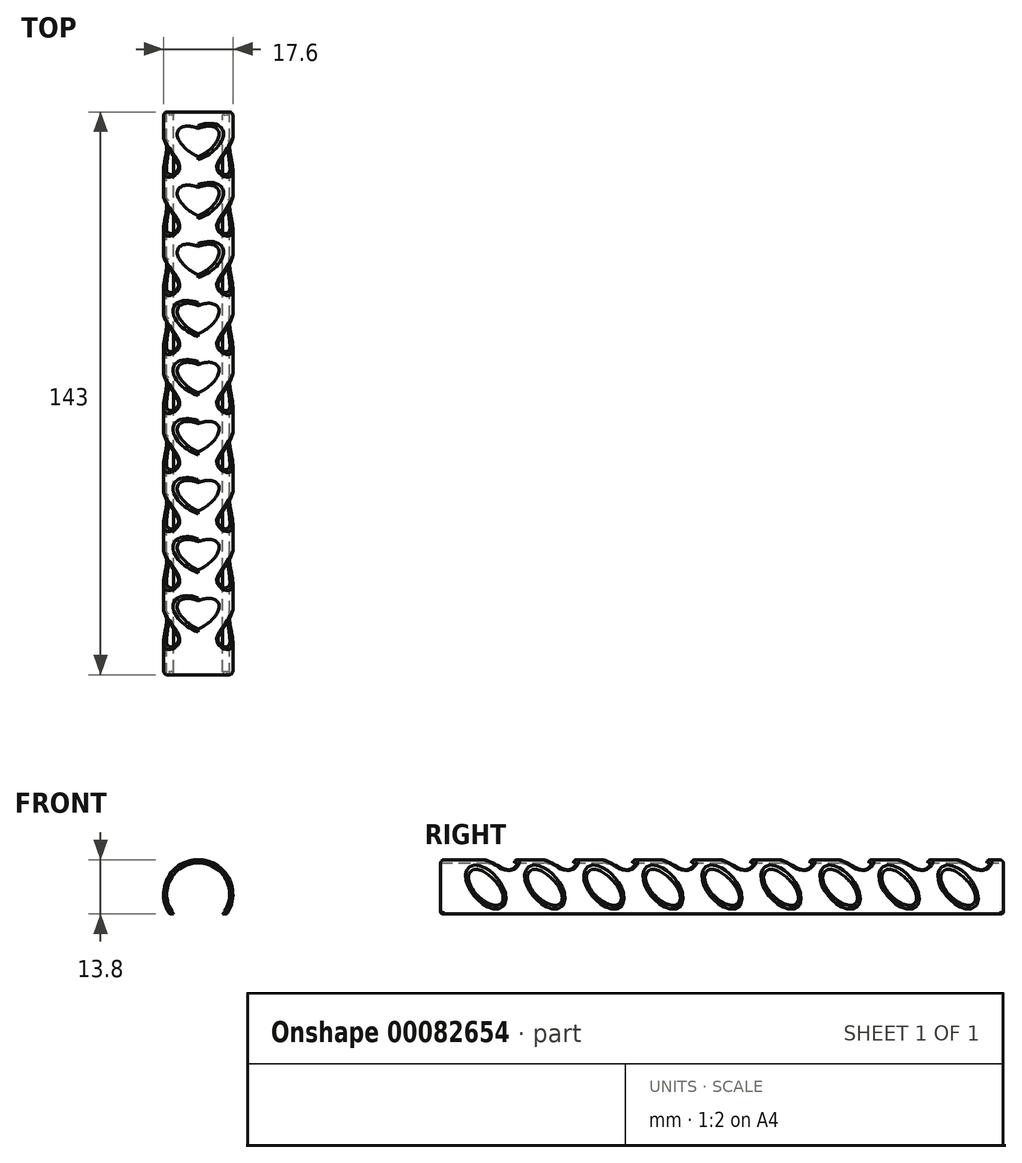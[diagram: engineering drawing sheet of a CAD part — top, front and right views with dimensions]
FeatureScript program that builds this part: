
annotation { "Feature Type Name" : "Feature", "Feature Type Description" : "" }
export const myFeature = defineFeature(function(context is Context, id is Id, definition is map)
    precondition{}
    {
        {
            var Q0;
            Q0=qCreatedBy(makeId("Front.planeOp"),FACE);
            var sketch = newSketch(context, id + "F0", { "sketchPlane" : qUnion([Q0])});
            skArc(sketch, "E0", {"start": v(6.24, -5) * mm, "mid": v(0, 8) * mm, "end": v(-6.24, -5) * mm});
            skArc(sketch, "E1", {"start": v(7.24, -5) * mm, "mid": v(0, 8.8) * mm, "end": v(-7.24, -5) * mm});
            skLineSegment(sketch, "E2", {"start": v(-7.24, -5) * mm, "end": v(-6.24, -5) * mm});
            skLineSegment(sketch, "E3.trimOffspring", {"start": v(6.24, -5) * mm, "end": v(7.24, -5) * mm});
            skSolve(sketch);
        }
        {
            var Q0;
            Q0 = qSketchRegion(id + "F0", true);
            extrude(context, id + "F1", {"entities" : qUnion([Q0]), "depth" : (143 / 2) * mm, "hasSecondDirection" : true, "secondDirectionOppositeDirection" : true, "secondDirectionDepth" : (143 / 2) * mm});
        }
        {
            var Q0;
            Q0=qCreatedBy(makeId("Right.planeOp"),FACE);
            var sketch = newSketch(context, id + "F2", { "sketchPlane" : qUnion([Q0])});
            skEllipse(sketch, "E4", {"center": v(0, 1.68) * mm, "majorRadius": 5.6 * mm, "minorRadius": 2.87 * mm, "majorAxis": v(0.7, -0.71)});
            skEllipse(sketch, "E5.1.0.0", {"center": v(15, 1.68) * mm, "majorRadius": 5.6 * mm, "minorRadius": 2.87 * mm, "majorAxis": v(0.7, -0.71)});
            skEllipse(sketch, "E5.2.0.0", {"center": v(30, 1.68) * mm, "majorRadius": 5.6 * mm, "minorRadius": 2.87 * mm, "majorAxis": v(0.7, -0.71)});
            skEllipse(sketch, "E5.3.0.0", {"center": v(45, 1.68) * mm, "majorRadius": 5.6 * mm, "minorRadius": 2.87 * mm, "majorAxis": v(0.7, -0.71)});
            skEllipse(sketch, "E5.4.0.0", {"center": v(60, 1.68) * mm, "majorRadius": 5.6 * mm, "minorRadius": 2.87 * mm, "majorAxis": v(0.7, -0.71)});
            skLineSegment(sketch, "E5.direction1", {"start": v(0, 1.68) * mm, "end": v(15, 1.68) * mm, "construction": true});
            skEllipse(sketch, "E6.1.0.0", {"center": v(-15, 1.68) * mm, "majorRadius": 5.6 * mm, "minorRadius": 2.87 * mm, "majorAxis": v(0.7, -0.71)});
            skEllipse(sketch, "E6.2.0.0", {"center": v(-30, 1.68) * mm, "majorRadius": 5.6 * mm, "minorRadius": 2.87 * mm, "majorAxis": v(0.7, -0.71)});
            skEllipse(sketch, "E6.3.0.0", {"center": v(-45, 1.68) * mm, "majorRadius": 5.6 * mm, "minorRadius": 2.87 * mm, "majorAxis": v(0.7, -0.71)});
            skEllipse(sketch, "E6.4.0.0", {"center": v(-60, 1.68) * mm, "majorRadius": 5.6 * mm, "minorRadius": 2.87 * mm, "majorAxis": v(0.7, -0.71)});
            skLineSegment(sketch, "E6.direction1", {"start": v(0, 1.68) * mm, "end": v(-15, 1.68) * mm, "construction": true});
            skSolve(sketch);
        }
        {
            var Q0;
            Q0 = qSketchRegion(id + "F2", true);
            extrude(context, id + "F3", {"entities" : qUnion([Q0]), "operationType" : NewBodyOperationType.REMOVE, "oppositeDirection" : true, "depth" : 25 * mm, "hasSecondDirection" : true, "secondDirectionOppositeDirection" : false, "secondDirectionDepth" : 25 * mm});
        }
        {
            var Q0;
            Q0=qCreatedBy(makeId("Top.planeOp"),FACE);
            var sketch = newSketch(context, id + "F4", { "sketchPlane" : qUnion([Q0])});
            skEllipticalArc(sketch, "E7", {});
            skLineSegment(sketch, "E8", {"start": v(0, 58.68) * mm, "end": v(0, 42.52) * mm, "construction": true});
            skEllipticalArc(sketch, "E9.MirrorCS", {});
            skEllipticalArc(sketch, "E10.0.1.0", {});
            skEllipticalArc(sketch, "E10.0.1.1", {});
            skEllipticalArc(sketch, "E10.0.2.0", {});
            skEllipticalArc(sketch, "E10.0.2.1", {});
            skEllipticalArc(sketch, "E10.0.3.0", {});
            skEllipticalArc(sketch, "E10.0.3.1", {});
            skEllipticalArc(sketch, "E10.0.4.0", {});
            skEllipticalArc(sketch, "E10.0.4.1", {});
            skEllipticalArc(sketch, "E10.0.5.0", {});
            skEllipticalArc(sketch, "E10.0.5.1", {});
            skEllipticalArc(sketch, "E10.0.6.0", {});
            skEllipticalArc(sketch, "E10.0.6.1", {});
            skEllipticalArc(sketch, "E10.0.7.0", {});
            skEllipticalArc(sketch, "E10.0.7.1", {});
            skLineSegment(sketch, "E10.direction1", {"start": v(0, 45.14) * mm, "end": v(25, 45.14) * mm, "construction": true});
            skLineSegment(sketch, "E10.direction2", {"start": v(0, 45.14) * mm, "end": v(0, 30.14) * mm, "construction": true});
            skEllipticalArc(sketch, "E11.0.1.0", {});
            skEllipticalArc(sketch, "E11.0.1.1", {});
            skLineSegment(sketch, "E11.direction2", {"start": v(0, 45.14) * mm, "end": v(0, 60.14) * mm, "construction": true});
            const initialGuessF4  = {"E7": [0, 0.04871673882007599, 0.8358285471048497, 0.5489905644404065, 0.005878045911660916, 0.003174595466172433, 4.371502825433306, 1.2299101718435133], "E9.MirrorCS": [0, 0.04871673882007599, -0.8358285471048497, 0.5489905644404065, 0.005878045911660916, 0.003174595466172433, 5.053275135336073, 1.91168248174628], "E10.0.1.0": [0, 0.03371673882007599, 0.8358285471048497, 0.5489905644404065, 0.005878045911660916, 0.003174595466172433, 4.371502825433306, 1.229910171843513], "E10.0.1.1": [0, 0.03371673882007599, -0.8358285471048497, 0.5489905644404065, 0.005878045911660916, 0.003174595466172433, 5.053275135336073, 1.91168248174628], "E10.0.2.0": [0, 0.01871673882007599, 0.8358285471048497, 0.5489905644404065, 0.005878045911660916, 0.003174595466172433, 4.371502825433306, 1.229910171843513], "E10.0.2.1": [0, 0.01871673882007599, -0.8358285471048497, 0.5489905644404065, 0.005878045911660916, 0.003174595466172433, 5.053275135336073, 1.91168248174628], "E10.0.3.0": [0, 0.0037167388200759904, 0.8358285471048497, 0.5489905644404065, 0.005878045911660916, 0.003174595466172433, 4.371502825433306, 1.229910171843513], "E10.0.3.1": [0, 0.0037167388200759904, -0.8358285471048497, 0.5489905644404065, 0.005878045911660916, 0.003174595466172433, 5.053275135336073, 1.91168248174628], "E10.0.4.0": [0, -0.011283261179924009, 0.8358285471048497, 0.5489905644404065, 0.005878045911660916, 0.003174595466172433, 4.371502825433306, 1.229910171843513], "E10.0.4.1": [0, -0.011283261179924009, -0.8358285471048497, 0.5489905644404065, 0.005878045911660916, 0.003174595466172433, 5.053275135336073, 1.91168248174628], "E10.0.5.0": [0, -0.02628326117992401, 0.8358285471048497, 0.5489905644404065, 0.005878045911660916, 0.003174595466172433, 4.371502825433306, 1.229910171843513], "E10.0.5.1": [0, -0.02628326117992401, -0.8358285471048497, 0.5489905644404065, 0.005878045911660916, 0.003174595466172433, 5.053275135336073, 1.91168248174628], "E10.0.6.0": [0, -0.04128326117992401, 0.8358285471048497, 0.5489905644404065, 0.005878045911660916, 0.003174595466172433, 4.371502825433306, 1.229910171843513], "E10.0.6.1": [0, -0.04128326117992401, -0.8358285471048497, 0.5489905644404065, 0.005878045911660916, 0.003174595466172433, 5.053275135336073, 1.91168248174628], "E10.0.7.0": [0, -0.05628326117992401, 0.8358285471048497, 0.5489905644404065, 0.005878045911660916, 0.003174595466172433, 4.371502825433306, 1.229910171843513], "E10.0.7.1": [0, -0.05628326117992401, -0.8358285471048497, 0.5489905644404065, 0.005878045911660916, 0.003174595466172433, 5.053275135336073, 1.91168248174628], "E11.0.1.0": [0, 0.06371673882007599, 0.8358285471048497, 0.5489905644404065, 0.005878045911660916, 0.003174595466172433, 4.371502825433306, 1.229910171843513], "E11.0.1.1": [0, 0.06371673882007599, -0.8358285471048497, 0.5489905644404065, 0.005878045911660916, 0.003174595466172433, 5.053275135336073, 1.91168248174628]};
            skSetInitialGuess(sketch, initialGuessF4);
            skSolve(sketch);
        }
        {
            var Q0;
            Q0 = qSketchRegion(id + "F4", true);
            extrude(context, id + "F5", {"entities" : qUnion([Q0]), "operationType" : NewBodyOperationType.REMOVE, "depth" : 25 * mm});
        }
        {
            var Q0;
            Q0=makeQuery(id+"F1.opExtrude","CAP_EDGE",EDGE,{"disambiguationData":[OSD([sQuery(id+"F0.wireOp",EDGE,"E1")])],"isStart":true});
            var Q1;
            Q1=makeQuery(id+"F1.opExtrude","CAP_EDGE",EDGE,{"disambiguationData":[OSD([sQuery(id+"F0.wireOp",EDGE,"E1")])],"isStart":false});
            fillet(context, id + "F6", {"entities" : qUnion([Q0, Q1]), "radius" : 1 * mm, "tangentPropagation" : true, "allowEdgeOverflow" : false});
        }
        {
            var Q0;
            Q0=makeQuery(id+"F3.boolean.opBoolean","INTERSECT",EDGE,{"disambiguationData":[OD(0.0)],"derivedFrom":[makeQuery(id+"F1.opExtrude","SWEPT_FACE",FACE,{"disambiguationData":[OSD([sQuery(id+"F0.wireOp",EDGE,"E1")])]}),makeQuery(id+"F3.opExtrude","SWEPT_FACE",FACE,{"disambiguationData":[OSD([sQuery(id+"F2.wireOp",EDGE,"E5.4.0.0")])]})]});
            var Q1;
            Q1=makeQuery(id+"F3.boolean.opBoolean","INTERSECT",EDGE,{"disambiguationData":[OD(0.0)],"derivedFrom":[makeQuery(id+"F1.opExtrude","SWEPT_FACE",FACE,{"disambiguationData":[OSD([sQuery(id+"F0.wireOp",EDGE,"E1")])]}),makeQuery(id+"F3.opExtrude","SWEPT_FACE",FACE,{"disambiguationData":[OSD([sQuery(id+"F2.wireOp",EDGE,"E5.3.0.0")])]})]});
            var Q2;
            Q2=makeQuery(id+"F3.boolean.opBoolean","INTERSECT",EDGE,{"disambiguationData":[OD(0.0)],"derivedFrom":[makeQuery(id+"F1.opExtrude","SWEPT_FACE",FACE,{"disambiguationData":[OSD([sQuery(id+"F0.wireOp",EDGE,"E1")])]}),makeQuery(id+"F3.opExtrude","SWEPT_FACE",FACE,{"disambiguationData":[OSD([sQuery(id+"F2.wireOp",EDGE,"E5.2.0.0")])]})]});
            var Q3;
            Q3=makeQuery(id+"F3.boolean.opBoolean","INTERSECT",EDGE,{"disambiguationData":[OD(0.0)],"derivedFrom":[makeQuery(id+"F1.opExtrude","SWEPT_FACE",FACE,{"disambiguationData":[OSD([sQuery(id+"F0.wireOp",EDGE,"E1")])]}),makeQuery(id+"F3.opExtrude","SWEPT_FACE",FACE,{"disambiguationData":[OSD([sQuery(id+"F2.wireOp",EDGE,"E5.1.0.0")])]})]});
            var Q4;
            Q4=makeQuery(id+"F3.boolean.opBoolean","INTERSECT",EDGE,{"disambiguationData":[OD(0.0)],"derivedFrom":[makeQuery(id+"F1.opExtrude","SWEPT_FACE",FACE,{"disambiguationData":[OSD([sQuery(id+"F0.wireOp",EDGE,"E1")])]}),makeQuery(id+"F3.opExtrude","SWEPT_FACE",FACE,{"disambiguationData":[OSD([sQuery(id+"F2.wireOp",EDGE,"E4")])]})]});
            var Q5;
            Q5=makeQuery(id+"F3.boolean.opBoolean","INTERSECT",EDGE,{"disambiguationData":[OD(0.0)],"derivedFrom":[makeQuery(id+"F1.opExtrude","SWEPT_FACE",FACE,{"disambiguationData":[OSD([sQuery(id+"F0.wireOp",EDGE,"E1")])]}),makeQuery(id+"F3.opExtrude","SWEPT_FACE",FACE,{"disambiguationData":[OSD([sQuery(id+"F2.wireOp",EDGE,"E6.1.0.0")])]})]});
            var Q6;
            Q6=makeQuery(id+"F3.boolean.opBoolean","INTERSECT",EDGE,{"disambiguationData":[OD(0.0)],"derivedFrom":[makeQuery(id+"F1.opExtrude","SWEPT_FACE",FACE,{"disambiguationData":[OSD([sQuery(id+"F0.wireOp",EDGE,"E1")])]}),makeQuery(id+"F3.opExtrude","SWEPT_FACE",FACE,{"disambiguationData":[OSD([sQuery(id+"F2.wireOp",EDGE,"E6.2.0.0")])]})]});
            var Q7;
            Q7=makeQuery(id+"F3.boolean.opBoolean","INTERSECT",EDGE,{"disambiguationData":[OD(0.0)],"derivedFrom":[makeQuery(id+"F1.opExtrude","SWEPT_FACE",FACE,{"disambiguationData":[OSD([sQuery(id+"F0.wireOp",EDGE,"E1")])]}),makeQuery(id+"F3.opExtrude","SWEPT_FACE",FACE,{"disambiguationData":[OSD([sQuery(id+"F2.wireOp",EDGE,"E6.3.0.0")])]})]});
            var Q8;
            Q8=makeQuery(id+"F3.boolean.opBoolean","INTERSECT",EDGE,{"disambiguationData":[OD(0.0)],"derivedFrom":[makeQuery(id+"F1.opExtrude","SWEPT_FACE",FACE,{"disambiguationData":[OSD([sQuery(id+"F0.wireOp",EDGE,"E1")])]}),makeQuery(id+"F3.opExtrude","SWEPT_FACE",FACE,{"disambiguationData":[OSD([sQuery(id+"F2.wireOp",EDGE,"E6.4.0.0")])]})]});
            var Q9;
            Q9=makeQuery(id+"F5.boolean.opBoolean","INTERSECT",EDGE,{"derivedFrom":[makeQuery(id+"F1.opExtrude","SWEPT_FACE",FACE,{"disambiguationData":[OSD([sQuery(id+"F0.wireOp",EDGE,"E1")])]}),makeQuery(id+"F5.opExtrude","SWEPT_FACE",FACE,{"disambiguationData":[OSD([sQuery(id+"F4.wireOp",EDGE,"E10.0.7.1")])]})]});
            var Q10;
            Q10=makeQuery(id+"F5.boolean.opBoolean","INTERSECT",EDGE,{"derivedFrom":[makeQuery(id+"F1.opExtrude","SWEPT_FACE",FACE,{"disambiguationData":[OSD([sQuery(id+"F0.wireOp",EDGE,"E1")])]}),makeQuery(id+"F5.opExtrude","SWEPT_FACE",FACE,{"disambiguationData":[OSD([sQuery(id+"F4.wireOp",EDGE,"E10.0.6.1")])]})]});
            var Q11;
            Q11=makeQuery(id+"F5.boolean.opBoolean","INTERSECT",EDGE,{"derivedFrom":[makeQuery(id+"F1.opExtrude","SWEPT_FACE",FACE,{"disambiguationData":[OSD([sQuery(id+"F0.wireOp",EDGE,"E1")])]}),makeQuery(id+"F5.opExtrude","SWEPT_FACE",FACE,{"disambiguationData":[OSD([sQuery(id+"F4.wireOp",EDGE,"E10.0.5.1")])]})]});
            var Q12;
            Q12=makeQuery(id+"F5.boolean.opBoolean","INTERSECT",EDGE,{"derivedFrom":[makeQuery(id+"F1.opExtrude","SWEPT_FACE",FACE,{"disambiguationData":[OSD([sQuery(id+"F0.wireOp",EDGE,"E1")])]}),makeQuery(id+"F5.opExtrude","SWEPT_FACE",FACE,{"disambiguationData":[OSD([sQuery(id+"F4.wireOp",EDGE,"E10.0.4.1")])]})]});
            var Q13;
            Q13=makeQuery(id+"F5.boolean.opBoolean","INTERSECT",EDGE,{"derivedFrom":[makeQuery(id+"F1.opExtrude","SWEPT_FACE",FACE,{"disambiguationData":[OSD([sQuery(id+"F0.wireOp",EDGE,"E1")])]}),makeQuery(id+"F5.opExtrude","SWEPT_FACE",FACE,{"disambiguationData":[OSD([sQuery(id+"F4.wireOp",EDGE,"E10.0.3.1")])]})]});
            var Q14;
            Q14=makeQuery(id+"F5.boolean.opBoolean","INTERSECT",EDGE,{"derivedFrom":[makeQuery(id+"F1.opExtrude","SWEPT_FACE",FACE,{"disambiguationData":[OSD([sQuery(id+"F0.wireOp",EDGE,"E1")])]}),makeQuery(id+"F5.opExtrude","SWEPT_FACE",FACE,{"disambiguationData":[OSD([sQuery(id+"F4.wireOp",EDGE,"E10.0.2.1")])]})]});
            var Q15;
            Q15=makeQuery(id+"F1.opExtrude","SWEPT_FACE",FACE,{"disambiguationData":[OSD([sQuery(id+"F0.wireOp",EDGE,"E1")])]});
            fillet(context, id + "F7", {"entities" : qUnion([Q0, Q1, Q2, Q3, Q4, Q5, Q6, Q7, Q8, Q9, Q10, Q11, Q12, Q13, Q14, Q15]), "radius" : .7 * mm, "tangentPropagation" : true, "allowEdgeOverflow" : false});
        }
    });
